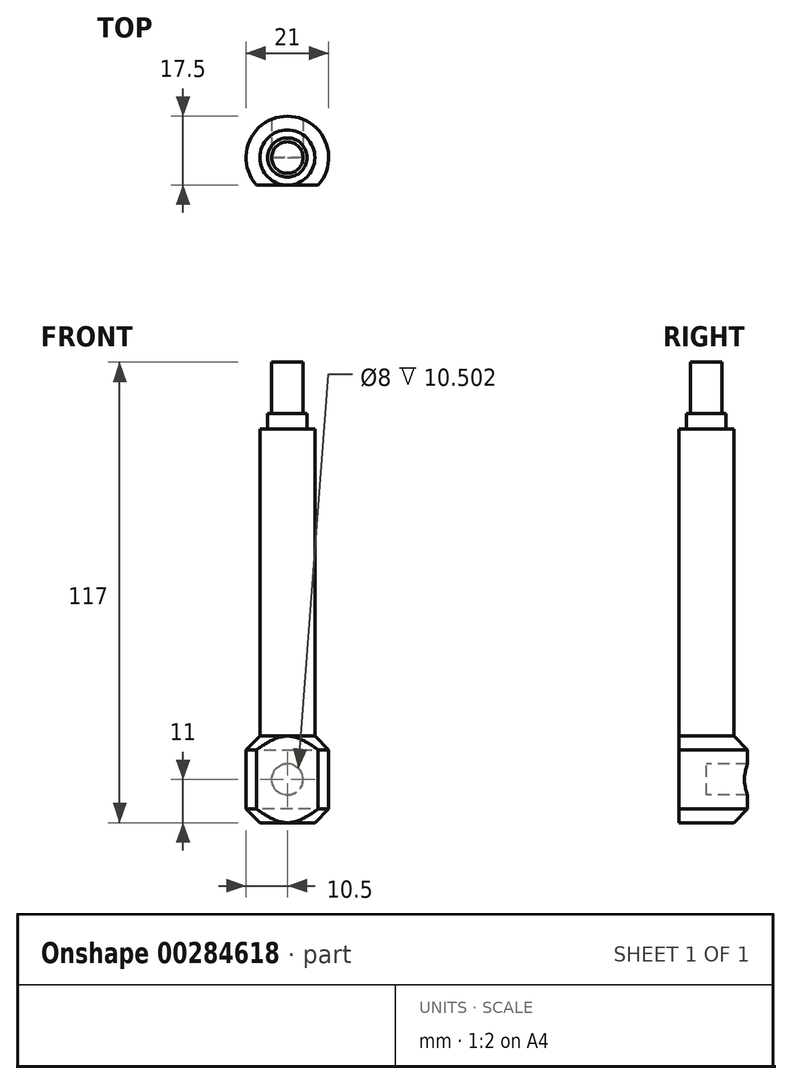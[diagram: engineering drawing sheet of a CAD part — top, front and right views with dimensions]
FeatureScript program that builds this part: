
annotation { "Feature Type Name" : "Feature", "Feature Type Description" : "" }
export const myFeature = defineFeature(function(context is Context, id is Id, definition is map)
    precondition{}
    {
        {
            var Q0;
            Q0=qCreatedBy(makeId("Front.planeOp"),FACE);
            var sketch = newSketch(context, id + "F0", { "sketchPlane" : qUnion([Q0])});
            skLineSegment(sketch, "E0", {"start": v(0, 0) * mm, "end": v(10.5, 0) * mm});
            skLineSegment(sketch, "E1", {"start": v(10.5, 0) * mm, "end": v(10.5, 22) * mm});
            skLineSegment(sketch, "E2", {"start": v(10.5, 22) * mm, "end": v(7, 22) * mm});
            skLineSegment(sketch, "E3", {"start": v(7, 22) * mm, "end": v(7, 100) * mm});
            skLineSegment(sketch, "E4", {"start": v(7, 100) * mm, "end": v(5, 100) * mm});
            skLineSegment(sketch, "E5", {"start": v(5, 100) * mm, "end": v(5, 104) * mm});
            skLineSegment(sketch, "E6", {"start": v(5, 104) * mm, "end": v(4, 104) * mm});
            skLineSegment(sketch, "E7", {"start": v(4, 104) * mm, "end": v(4, 117) * mm});
            skLineSegment(sketch, "E8", {"start": v(4, 117) * mm, "end": v(0, 117) * mm});
            skLineSegment(sketch, "E9", {"start": v(0, 117) * mm, "end": v(0, 0) * mm});
            skLineSegment(sketch, "E10", {"start": v(0, 117) * mm, "end": v(0, 0) * mm, "construction": true});
            skSolve(sketch);
        }
        {
            var Q0;
            Q0 = qSketchRegion(id + "F0", true);
            var Q1;
            Q1=sQuery(id+"F0.wireOp",EDGE,"E9");
            revolve(context, id + "F1", {"entities" : qUnion([Q0]), "axis" : qUnion([Q1]), "revolveType" : RevolveType.FULL});
        }
        {
            var Q0;
            Q0=qCreatedBy(makeId("Front.planeOp"),FACE);
            var sketch = newSketch(context, id + "F2", { "sketchPlane" : qUnion([Q0])});
            skLineSegment(sketch, "E11", {"start": v(-10.5, 0) * mm, "end": v(-10.5, 22) * mm, "construction": true});
            skLineSegment(sketch, "E12", {"start": v(10.5, 22) * mm, "end": v(10.5, 0) * mm, "construction": true});
            skLineSegment(sketch, "E13", {"start": v(0, 0) * mm, "end": v(0, 28.11) * mm, "construction": true});
            skLineSegment(sketch, "E14", {"start": v(-10.5, 11) * mm, "end": v(10.5, 11) * mm, "construction": true});
            skPoint(sketch, "E15", {"position": v(0, 11) * mm});
            skSolve(sketch);
        }
        {
            var Q0;
            Q0=sQuery(id+"F2.wireOp",VERTEX,"E15");
            var Q1;
            Q1=makeQuery(id+"F1.opRevolve","SWEPT_BODY",BODY,{"disambiguationData":[OSD([sQuery(id+"F0.wireOp",EDGE,"E0"),sQuery(id+"F0.wireOp",EDGE,"E1"),sQuery(id+"F0.wireOp",EDGE,"E2"),sQuery(id+"F0.wireOp",EDGE,"E3"),sQuery(id+"F0.wireOp",EDGE,"E4"),sQuery(id+"F0.wireOp",EDGE,"E5"),sQuery(id+"F0.wireOp",EDGE,"E6"),sQuery(id+"F0.wireOp",EDGE,"E7"),sQuery(id+"F0.wireOp",EDGE,"E8"),sQuery(id+"F0.wireOp",EDGE,"E9")])]});
            hole(context, id + "F3", {"style" : HoleStyle.SIMPLE, "endStyle" : HoleEndStyle.THROUGH, "holeDiameter" : 8 * mm, "tappedDepth" : 12 * mm, "tapClearance" : 3, "locations" : qUnion([Q0]), "scope" : qUnion([Q1])});
        }
        {
            var Q0;
            Q0=qCreatedBy(makeId("Front.planeOp"),FACE);
            cPlane(context, id + "F4", {"entities" : qUnion([Q0]), "cplaneType" : CPlaneType.OFFSET, "offset" : 7 * mm, "width" : 150 * mm, "height" : 150 * mm});
        }
        {
            var Q0;
            Q0=qCreatedBy(id+"F4.planeOp",FACE);
            var sketch = newSketch(context, id + "F5", { "sketchPlane" : qUnion([Q0])});
            skLineSegment(sketch, "E16.bottom", {"start": v(-12.1, 22) * mm, "end": v(13.39, 22) * mm});
            skLineSegment(sketch, "E16.top", {"start": v(-12.1, 0) * mm, "end": v(13.39, 0) * mm});
            skLineSegment(sketch, "E16.left", {"start": v(-12.1, 22) * mm, "end": v(-12.1, 0) * mm});
            skLineSegment(sketch, "E16.right", {"start": v(13.39, 22) * mm, "end": v(13.39, 0) * mm});
            skLineSegment(sketch, "E17", {"start": v(-7.83, 0) * mm, "end": v(-7.83, 22) * mm, "construction": true});
            skLineSegment(sketch, "E18", {"start": v(7.83, 22) * mm, "end": v(7.83, 0) * mm, "construction": true});
            skLineSegment(sketch, "E19", {"start": v(0, 100) * mm, "end": v(0, 22) * mm, "construction": true});
            skLineSegment(sketch, "E20", {"start": v(-7.83, 0) * mm, "end": v(-7.83, 22) * mm});
            skLineSegment(sketch, "E21", {"start": v(7.83, 22) * mm, "end": v(7.83, 0) * mm});
            skSolve(sketch);
        }
        {
            var Q0;
            Q0 = qSketchRegion(id + "F5", true);
            extrude(context, id + "F6", {"entities" : qUnion([Q0]), "operationType" : NewBodyOperationType.REMOVE, "endBound" : BoundingType.THROUGH_ALL, "depth" : 25 * mm});
        }
        {
            var Q0;
            Q0=makeQuery(id+"FCb6IwEKzA1KBKa_1.1.F6.boolean.opBoolean","SPLIT",EDGE,{"disambiguationData":[OD(1.0)],"derivedFrom":makeQuery(id+"F1.opRevolve","SWEPT_EDGE",EDGE,{"disambiguationData":[OSD([sQuery(id+"F0.wireOp",EDGE,"E1"),sQuery(id+"F0.wireOp",EDGE,"E2")])]})});
            var Q1;
            Q1=makeQuery(id+"FCb6IwEKzA1KBKa_1.1.F6.boolean.opBoolean","SPLIT",EDGE,{"disambiguationData":[OD(0.0)],"derivedFrom":makeQuery(id+"F1.opRevolve","SWEPT_EDGE",EDGE,{"disambiguationData":[OSD([sQuery(id+"F0.wireOp",EDGE,"E1"),sQuery(id+"F0.wireOp",EDGE,"E2")])]})});
            var Q2;
            Q2=makeQuery(id+"FCb6IwEKzA1KBKa_1.1.F6.boolean.opBoolean","SPLIT",EDGE,{"disambiguationData":[OD(1.0)],"derivedFrom":makeQuery(id+"F1.opRevolve","SWEPT_EDGE",EDGE,{"disambiguationData":[OSD([sQuery(id+"F0.wireOp",EDGE,"E0"),sQuery(id+"F0.wireOp",EDGE,"E1")])]})});
            var Q3;
            Q3=makeQuery(id+"FCb6IwEKzA1KBKa_1.1.F6.boolean.opBoolean","SPLIT",EDGE,{"disambiguationData":[OD(0.0)],"derivedFrom":makeQuery(id+"F1.opRevolve","SWEPT_EDGE",EDGE,{"disambiguationData":[OSD([sQuery(id+"F0.wireOp",EDGE,"E0"),sQuery(id+"F0.wireOp",EDGE,"E1")])]})});
            chamfer(context, id + "F7", {"entities" : qUnion([Q0, Q1, Q2, Q3]), "width" : 3.5 * mm, "tangentPropagation" : true});
        }
    });
